# Revit family: 304_R206B-_
name_source: partatom
category: Pipe Accessories
revit_build: Autodesk Revit 2018 (Build: 20170223_1515(x64)
units: mm (PartAtom-declared; Revit-internal decimal feet)

## family parameters
Always vertical = Yes
Cut with Voids When Loaded = No
Part Type = Valve - Breaks Into
Round Connector Dimension = Use Diameter
Shared = No
Work Plane-Based = No

## types (6) — shared parameters
CAT0 = Yes
Description = Static balancing valve, female-female, with probe holder
H31 = 10 mm  [stored 0.0328084 ft]
H32 = 25 mm  [stored 0.082021 ft]
H33 = 7 mm  [stored 0.0229659 ft]
H4 = 20 mm  [stored 0.0656168 ft]
H6 = 60 mm
I = 25 mm  [stored 0.082021 ft]
L2D_Min = 3048 mm
Manufacturer = Giacomini
QmdConnectorList = 301;D;302;D
R4 = 8 mm  [stored 0.0262467 ft]
URL = http://www.giacomini.com
magiPartTypeId = 304
magiProductFamilyId = R206B-*
zero-valued in all types: MC_Default_elevation

## per-type parameters (varying)
- R206BY003: CenSd_NUT_6=13 mm; D=15 mm; H13=20 mm  [stored 0.0656168 ft]; H13__ve=-20 mm  [stored -0.0656168 ft]; H5=35 mm; L2=48 mm; L2D=95 mm; L3=13 mm; L3__ve=-13 mm; L4=8 mm  [stored 0.0262467 ft]; L4__ve=-8 mm  [stored -0.0262467 ft]; L5=10 mm  [stored 0.0328084 ft]; L5__ve=-10 mm  [stored -0.0328084 ft]; L6=34 mm; NUT=15 mm  [stored 0.0492126 ft]; P2=32 mm; P3=19 mm; P4=17 mm; P5=14 mm  [stored 0.0459318 ft]; R1=13 mm; R2=12 mm  [stored 0.0393701 ft]; R3=11 mm; SS=4 mm  [stored 0.0131234 ft]; W2D=15 mm  [stored 0.0492126 ft]; magiProductId=R206B-15
- R206BY008: CenSd_NUT_6=32 mm; D=50 mm; H13=40 mm; H13__ve=-40 mm; H5=73 mm; L2=77 mm; L2D=154 mm; L3=22 mm; L3__ve=-22 mm; L4=12 mm  [stored 0.0393701 ft]; L4__ve=-12 mm  [stored -0.0393701 ft]; L5=15 mm  [stored 0.0492126 ft]; L5__ve=-15 mm  [stored -0.0492126 ft]; L6=55 mm; NUT=38 mm; P2=35 mm; P3=20 mm  [stored 0.0656168 ft]; P4=19 mm; P5=16 mm  [stored 0.0524934 ft]; R1=32 mm; R2=30 mm; R3=27 mm; SS=17 mm; W2D=50 mm; magiProductId=R206B-50
- R206BY007: CenSd_NUT_6=25 mm  [stored 0.082021 ft]; D=40 mm; H13=34 mm; H13__ve=-34 mm; H5=73 mm; L2=70 mm; L2D=140 mm; L3=20 mm  [stored 0.0656168 ft]; L3__ve=-20 mm  [stored -0.0656168 ft]; L4=11 mm; L4__ve=-11 mm; L5=14 mm  [stored 0.0459318 ft]; L5__ve=-14 mm; L6=50 mm; NUT=29 mm; P2=32 mm; P3=19 mm; P4=17 mm; P5=14 mm  [stored 0.0459318 ft]; R1=25 mm  [stored 0.082021 ft]; R2=23 mm; R3=21 mm; SS=13 mm; W2D=40 mm; magiProductId=R206B-40
- R206BY006: CenSd_NUT_6=23 mm; D=32 mm; H13=30 mm; H13__ve=-30 mm; H5=35 mm; L2=60 mm; L2D=120 mm; L3=17 mm; L3__ve=-17 mm; L4=10 mm  [stored 0.0328084 ft]; L4__ve=-10 mm  [stored -0.0328084 ft]; L5=12 mm  [stored 0.0393701 ft]; L5__ve=-12 mm  [stored -0.0393701 ft]; L6=43 mm; NUT=26 mm; P2=32 mm; P3=19 mm; P4=17 mm; P5=14 mm  [stored 0.0459318 ft]; R1=22 mm; R2=21 mm; R3=19 mm; SS=10 mm  [stored 0.0328084 ft]; W2D=32 mm; magiProductId=R206B-32
- R206BY005: CenSd_NUT_6=20 mm  [stored 0.0656168 ft]; D=25 mm; H13=27 mm; H13__ve=-27 mm; H5=31 mm; L2=55 mm; L2D=110 mm; L3=15 mm  [stored 0.0492126 ft]; L3__ve=-15 mm  [stored -0.0492126 ft]; L4=9 mm  [stored 0.0295276 ft]; L4__ve=-9 mm; L5=11 mm; L5__ve=-11 mm; L6=40 mm; NUT=23 mm; P2=32 mm; P3=19 mm; P4=17 mm; P5=14 mm  [stored 0.0459318 ft]; R1=20 mm  [stored 0.0656168 ft]; R2=18 mm; R3=17 mm; SS=16 mm  [stored 0.0524934 ft]; W2D=25 mm  [stored 0.082021 ft]; magiProductId=R206B-25
- R206BY004: CenSd_NUT_6=16 mm  [stored 0.0524934 ft]; D=20 mm; H13=23 mm; H13__ve=-23 mm; H5=31 mm; L2=51 mm; L2D=101 mm; L3=14 mm  [stored 0.0459318 ft]; L3__ve=-14 mm; L4=8 mm  [stored 0.0262467 ft]; L4__ve=-8 mm  [stored -0.0262467 ft]; L5=10 mm  [stored 0.0328084 ft]; L5__ve=-10 mm  [stored -0.0328084 ft]; L6=36 mm; NUT=19 mm; P2=32 mm; P3=19 mm; P4=17 mm; P5=14 mm  [stored 0.0459318 ft]; R1=16 mm  [stored 0.0524934 ft]; R2=15 mm  [stored 0.0492126 ft]; R3=13 mm; SS=5 mm  [stored 0.0164042 ft]; W2D=20 mm  [stored 0.0656168 ft]; magiProductId=R206B-20

note: column(s) folded — value = type name in every type: magiProductCode

note: [stored X ft] marks values corroborated as IEEE doubles in the binary element streams (Revit-internal decimal feet)

## geometry (parser evidence)
native form markers: Sweep x1
no freeform markers — native parametric forms only
